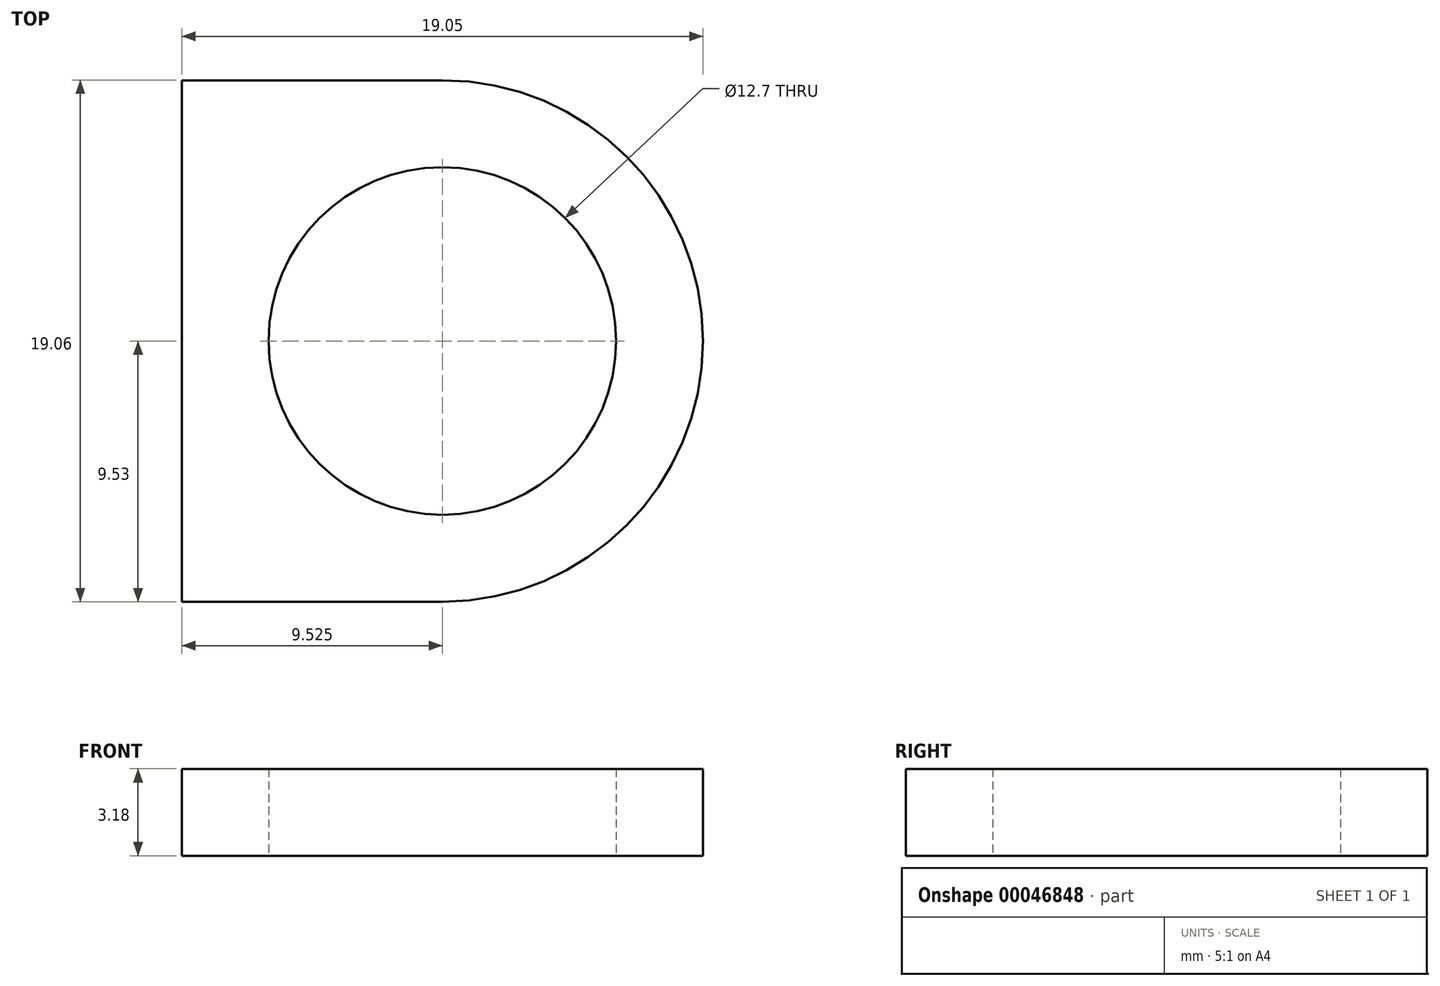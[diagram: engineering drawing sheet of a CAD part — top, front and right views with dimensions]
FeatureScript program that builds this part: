
annotation { "Feature Type Name" : "Feature", "Feature Type Description" : "" }
export const myFeature = defineFeature(function(context is Context, id is Id, definition is map)
    precondition{}
    {
        {
            var Q0;
            Q0=qCreatedBy(makeId("Top.planeOp"),FACE);
            var sketch = newSketch(context, id + "F0", { "sketchPlane" : qUnion([Q0])});
            skLineSegment(sketch, "E0", {"start": v(0, -9.53) * mm, "end": v(0, 9.53) * mm});
            skCircle(sketch, "E1", {"center": v(9.53, 0) * mm, "radius": 6.35 * mm});
            skLineSegment(sketch, "E2", {"start": v(0, 9.53) * mm, "end": v(9.53, 9.53) * mm});
            skLineSegment(sketch, "E3", {"start": v(0, -9.53) * mm, "end": v(9.53, -9.53) * mm});
            skArc(sketch, "E4", {"start": v(9.53, -9.53) * mm, "mid": v(19.05, 0) * mm, "end": v(9.53, 9.53) * mm});
            skSolve(sketch);
        }
        {
            var Q0;
            Q0=makeQuery(id+"F0.imprint","IMPRINT",FACE,{"disambiguationData":[TD([[makeQuery(id+"F0.imprint","IMPRINT",EDGE,{"derivedFrom":sQuery(id+"F0.wireOp",EDGE,"E0")}),-1.0]])]});
            extrude(context, id + "F1", {"entities" : qUnion([Q0]), "depth" : 3.17 * mm});
        }
    });
